# Revit family: basic_set_for_quattro_four_way_diverter_valve_for_concealed_installation_15930180_
name_source: partatom
category: Plumbing Fixtures
revit_build: Autodesk Revit 2015 (Build: 20140903_1530(x64)
units: mm (PartAtom-declared; Revit-internal decimal feet)

## types (1)
- n.a.
    BIMobject category = Valves
    BOSUseNativeGeometries = 1
    Brand url = http://www.hansgrohe-int.com
    Default Elevation = 4' - 0"
    Design country = Germany
    EAN code = https://4011097345239
    Edition number = 1
    IFC Classification = Valve
    Installation instructions = https://pro.hansgrohe-int.com
    Manufacturer country = Germany
    Manufacturer name = hansgrohe
    Masterformat 2014 Code = 33 12 16
    Masterformat 2014 Description = Water Utility Distribution Valves
    NBS Reference Code = 94
    NBS Reference Description = Valves
    Nominal height = 0
    Nominal width = 0
    OmniClass Code = 23-31 11 19 11
    OmniClass Description = Thermostatically Controlled Faucet Mixing Valves
    Product Guid = f083b1d0-8c90-4021-90f7-e0478d856c5e
    Product SKU = 15930180
    Product data url = https://bimobject.com
    Product family = Basic Sets
    Product group = Thermostatic mixers/valves
    Product name = Basic set for Quattro four-way diverter valve for concealed installation 15930180
    Product url = https://pro.hansgrohe-int.com
    QR code = http://bimobject.com
    Technical description = https://pro.hansgrohe-int.com
    UNSPSC Code = 40141616
    Uniclass 1.4 Code = L7117
    Uniclass 1.4 Description = Valves for water supply/distribution
    Uniclass 2.0 Code = PR-94-94-xx
    Uniclass 2.0 Description = Thermostatic Mixing Valves
    Uniclass 2015 Code = Pr_65_54
    Uniclass 2015 Name = Valve products
    Uniformat II Code = D20
    Uniformat II Description = PLUMBING
    Weight Net (Kg) = 0

## geometry (parser evidence)
native form markers: Sweep x2
no freeform markers — native parametric forms only
